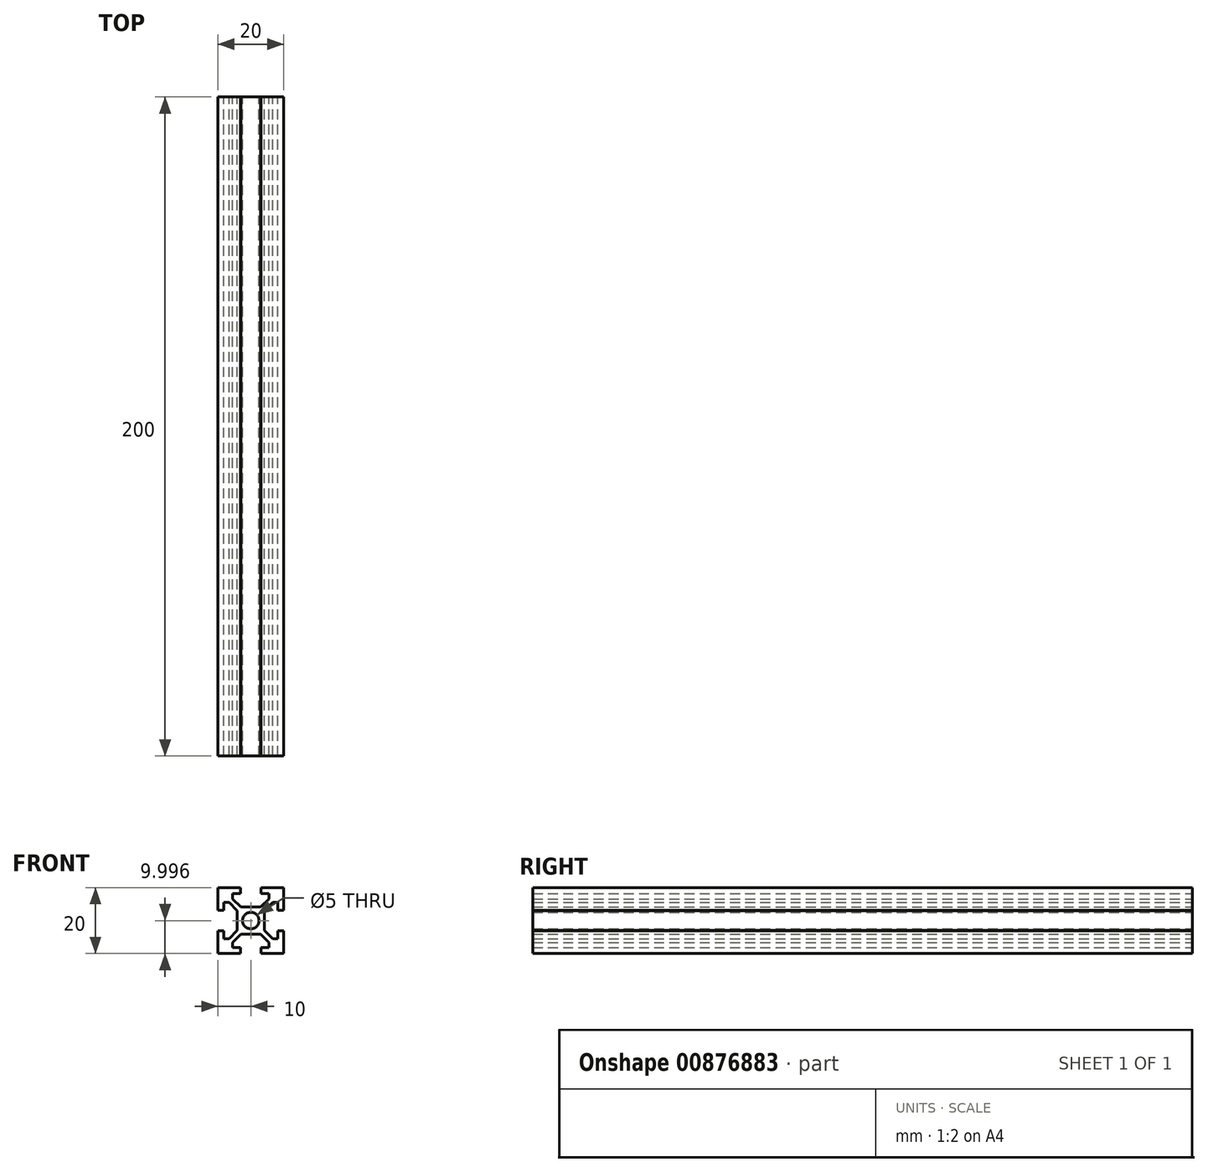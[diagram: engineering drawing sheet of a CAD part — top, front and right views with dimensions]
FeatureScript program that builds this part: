
annotation { "Feature Type Name" : "Feature", "Feature Type Description" : "" }
export const myFeature = defineFeature(function(context is Context, id is Id, definition is map)
    precondition{}
    {
        {
            var Q0;
            Q0=qCreatedBy(makeId("Front.planeOp"),FACE);
            var sketch = newSketch(context, id + "F0", { "sketchPlane" : qUnion([Q0])});
            skLineSegment(sketch, "E0.bottom", {"start": v(-26.4, 50.57) * mm, "end": v(-6.4, 50.57) * mm});
            skLineSegment(sketch, "E0.top", {"start": v(-26.4, 30.57) * mm, "end": v(-6.4, 30.57) * mm});
            skLineSegment(sketch, "E0.left", {"start": v(-26.4, 50.57) * mm, "end": v(-26.4, 30.57) * mm});
            skLineSegment(sketch, "E0.right", {"start": v(-6.4, 50.57) * mm, "end": v(-6.4, 30.57) * mm});
            skPoint(sketch, "E0.middle", {"position": v(-16.4, 40.57) * mm});
            skLineSegment(sketch, "E1", {"start": v(-8.2, 43.67) * mm, "end": v(-6.4, 43.67) * mm});
            skLineSegment(sketch, "E2.MirrorCS", {"start": v(-8.2, 37.47) * mm, "end": v(-6.4, 37.47) * mm});
            skLineSegment(sketch, "E3", {"start": v(-8.2, 43.67) * mm, "end": v(-8.2, 46.07) * mm});
            skLineSegment(sketch, "E4.MirrorCS", {"start": v(-8.2, 37.47) * mm, "end": v(-8.2, 35.07) * mm});
            skLineSegment(sketch, "E5", {"start": v(-8.2, 46.07) * mm, "end": v(-9.8, 46.07) * mm});
            skLineSegment(sketch, "E6.MirrorCS", {"start": v(-8.2, 35.07) * mm, "end": v(-9.8, 35.07) * mm});
            skCircle(sketch, "E7", {"center": v(-16.4, 40.57) * mm, "radius": 2.5 * mm});
            skLineSegment(sketch, "E8", {"start": v(-12.3, 43.57) * mm, "end": v(-12.3, 37.57) * mm});
            skLineSegment(sketch, "E9", {"start": v(-12.3, 43.57) * mm, "end": v(-9.8, 46.07) * mm});
            skLineSegment(sketch, "E10.MirrorCS", {"start": v(-12.3, 37.57) * mm, "end": v(-9.8, 35.07) * mm});
            skLineSegment(sketch, "E11.MirrorCS", {"start": v(-24.6, 43.67) * mm, "end": v(-26.4, 43.67) * mm});
            skLineSegment(sketch, "E12.MirrorCS", {"start": v(-24.6, 43.67) * mm, "end": v(-24.6, 46.07) * mm});
            skLineSegment(sketch, "E13.MirrorCS", {"start": v(-24.6, 46.07) * mm, "end": v(-23, 46.07) * mm});
            skLineSegment(sketch, "E14.MirrorCS", {"start": v(-20.5, 43.57) * mm, "end": v(-23, 46.07) * mm});
            skLineSegment(sketch, "E15.MirrorCS", {"start": v(-20.5, 43.57) * mm, "end": v(-20.5, 37.57) * mm});
            skLineSegment(sketch, "E16.MirrorCS", {"start": v(-20.5, 37.57) * mm, "end": v(-23, 35.07) * mm});
            skLineSegment(sketch, "E17.MirrorCS", {"start": v(-24.6, 35.07) * mm, "end": v(-23, 35.07) * mm});
            skLineSegment(sketch, "E18.MirrorCS", {"start": v(-24.6, 37.47) * mm, "end": v(-24.6, 35.07) * mm});
            skLineSegment(sketch, "E19.MirrorCS", {"start": v(-24.6, 37.47) * mm, "end": v(-26.4, 37.47) * mm});
            skLineSegment(sketch, "E20", {"start": v(-19.5, 50.57) * mm, "end": v(-19.5, 48.77) * mm});
            skLineSegment(sketch, "E21", {"start": v(-19.5, 48.77) * mm, "end": v(-21.9, 48.77) * mm});
            skLineSegment(sketch, "E22", {"start": v(-21.9, 48.77) * mm, "end": v(-21.9, 47.17) * mm});
            skLineSegment(sketch, "E23", {"start": v(-19.4, 44.67) * mm, "end": v(-16.4, 44.67) * mm});
            skLineSegment(sketch, "E24.MirrorCS", {"start": v(-13.3, 50.57) * mm, "end": v(-13.3, 48.77) * mm});
            skLineSegment(sketch, "E25.MirrorCS", {"start": v(-13.3, 48.77) * mm, "end": v(-10.9, 48.77) * mm});
            skLineSegment(sketch, "E26.MirrorCS", {"start": v(-10.9, 48.77) * mm, "end": v(-10.9, 47.17) * mm});
            skLineSegment(sketch, "E27.MirrorCS", {"start": v(-13.4, 44.67) * mm, "end": v(-16.4, 44.67) * mm});
            skLineSegment(sketch, "E28", {"start": v(-10.9, 47.17) * mm, "end": v(-13.4, 44.67) * mm});
            skLineSegment(sketch, "E29", {"start": v(-21.9, 47.17) * mm, "end": v(-19.4, 44.67) * mm});
            skLineSegment(sketch, "E30.MirrorCS", {"start": v(-19.5, 30.57) * mm, "end": v(-19.5, 32.37) * mm});
            skLineSegment(sketch, "E31.MirrorCS", {"start": v(-19.5, 32.37) * mm, "end": v(-21.9, 32.37) * mm});
            skLineSegment(sketch, "E32.MirrorCS", {"start": v(-21.9, 32.37) * mm, "end": v(-21.9, 33.97) * mm});
            skLineSegment(sketch, "E33.MirrorCS", {"start": v(-21.9, 33.97) * mm, "end": v(-19.4, 36.47) * mm});
            skLineSegment(sketch, "E34.MirrorCS", {"start": v(-13.3, 30.57) * mm, "end": v(-13.3, 32.37) * mm});
            skLineSegment(sketch, "E35.MirrorCS", {"start": v(-13.3, 32.37) * mm, "end": v(-10.9, 32.37) * mm});
            skLineSegment(sketch, "E36.MirrorCS", {"start": v(-10.9, 32.37) * mm, "end": v(-10.9, 33.97) * mm});
            skLineSegment(sketch, "E37.MirrorCS", {"start": v(-10.9, 33.97) * mm, "end": v(-13.4, 36.47) * mm});
            skLineSegment(sketch, "E38.MirrorCS", {"start": v(-13.4, 36.47) * mm, "end": v(-16.4, 36.47) * mm});
            skLineSegment(sketch, "E39.MirrorCS", {"start": v(-19.4, 36.47) * mm, "end": v(-16.4, 36.47) * mm});
            skSolve(sketch);
        }
        {
            var Q0;
            {var subQ5=sQuery(id+"F0.wireOp",EDGE,"c88a78db-e5ef-419d-bf41-abf41310455d");Q0=makeQuery(id+"F0.imprint","IMPRINT",FACE,{"disambiguationData":[TD([[makeQuery(id+"F0.imprint","IMPRINT",EDGE,{"derivedFrom":subQ5}),1.0]])]});}
            var Q1;
            {var subQ5=sQuery(id+"F0.wireOp",EDGE,"25cd5a18-daf1-494f-9de8-89f7957e7147");Q1=makeQuery(id+"F0.imprint","IMPRINT",FACE,{"disambiguationData":[TD([[makeQuery(id+"F0.imprint","IMPRINT",EDGE,{"derivedFrom":subQ5}),1.0]])]});}
            var Q2;
            {var subQ5=sQuery(id+"F0.wireOp",EDGE,"E1");Q2=makeQuery(id+"F0.imprint","IMPRINT",FACE,{"disambiguationData":[TD([[makeQuery(id+"F0.imprint","IMPRINT",EDGE,{"derivedFrom":subQ5}),1.0]])]});}
            var Q3;
            {var subQ5=sQuery(id+"F0.wireOp",EDGE,"60c817c8-cc4d-439b-9882-6d11aed29188");Q3=makeQuery(id+"F0.imprint","IMPRINT",FACE,{"disambiguationData":[TD([[makeQuery(id+"F0.imprint","IMPRINT",EDGE,{"derivedFrom":subQ5}),1.0]])]});}
            var Q4;
            {var subQ5=sQuery(id+"F0.wireOp",EDGE,"0c505c17-bd85-4911-bcb9-06047c46e684");Q4=makeQuery(id+"F0.imprint","IMPRINT",FACE,{"disambiguationData":[TD([[makeQuery(id+"F0.imprint","IMPRINT",EDGE,{"derivedFrom":subQ5}),1.0]])]});}
            var Q5;
            {var subQ5=sQuery(id+"F0.wireOp",EDGE,"3294ae28-d003-45a7-a1e9-691dd403ca17");Q5=makeQuery(id+"F0.imprint","IMPRINT",FACE,{"disambiguationData":[TD([[makeQuery(id+"F0.imprint","IMPRINT",EDGE,{"derivedFrom":subQ5}),1.0]])]});}
            extrude(context, id + "F1", {"entities" : qUnion([Q0, Q1, Q2, Q3, Q4, Q5]), "depth" : 200 * mm, "offsetDistance" : 25 * mm});
        }
    });
